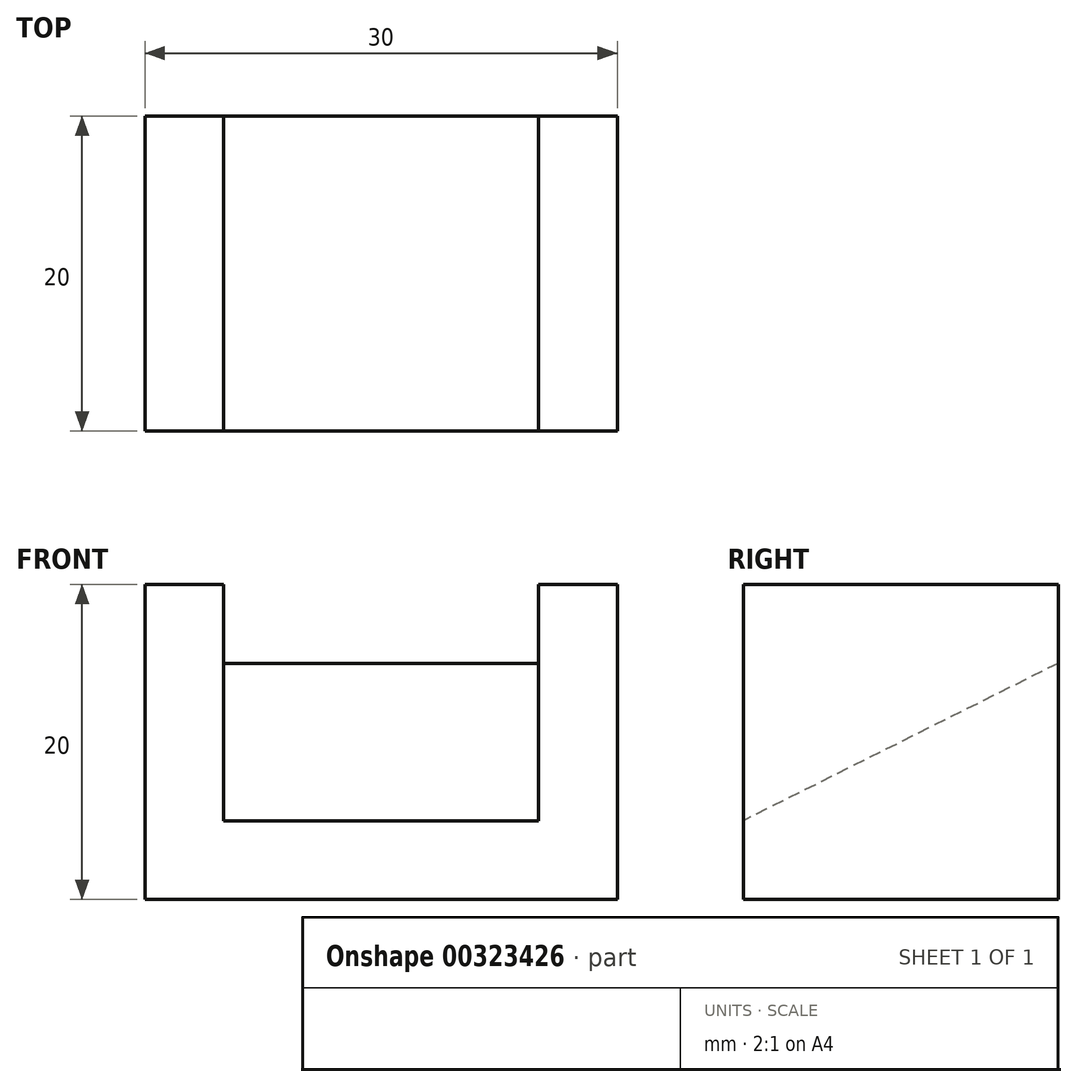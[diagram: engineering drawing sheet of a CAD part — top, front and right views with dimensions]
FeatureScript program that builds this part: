
annotation { "Feature Type Name" : "Feature", "Feature Type Description" : "" }
export const myFeature = defineFeature(function(context is Context, id is Id, definition is map)
    precondition{}
    {
        {
            var Q0;
            Q0=qCreatedBy(makeId("Front.planeOp"),FACE);
            var sketch = newSketch(context, id + "F0", { "sketchPlane" : qUnion([Q0])});
            skLineSegment(sketch, "E0.bottom", {"start": v(0, 0) * mm, "end": v(5, 0) * mm});
            skLineSegment(sketch, "E0.top", {"start": v(0, 20) * mm, "end": v(5, 20) * mm});
            skLineSegment(sketch, "E0.left", {"start": v(0, 0) * mm, "end": v(0, 20) * mm});
            skLineSegment(sketch, "E0.right", {"start": v(5, 0) * mm, "end": v(5, 20) * mm});
            skSolve(sketch);
        }
        {
            var Q0;
            Q0 = qSketchRegion(id + "F0", true);
            extrude(context, id + "F1", {"entities" : qUnion([Q0]), "depth" : 20 * mm});
        }
        {
            var Q0;
            Q0=makeQuery(id+"F1.opExtrude","SWEPT_FACE",FACE,{"disambiguationData":[OSD([sQuery(id+"F0.wireOp",EDGE,"E0.right")])]});
            var sketch = newSketch(context, id + "F2", { "sketchPlane" : qUnion([Q0])});
            skLineSegment(sketch, "E1", {"start": v(0, 15) * mm, "end": v(-20, 5) * mm});
            skLineSegment(sketch, "E2", {"start": v(-20, 5) * mm, "end": v(0, 5) * mm});
            skLineSegment(sketch, "E3", {"start": v(0, 5) * mm, "end": v(0, 15) * mm});
            skSolve(sketch);
        }
        {
            var Q0;
            Q0=makeQuery(id+"F2.imprint","IMPRINT",FACE,{"disambiguationData":[TD([[makeQuery(id+"F2.imprint","IMPRINT",EDGE,{"derivedFrom":sQuery(id+"F2.wireOp",EDGE,"E1")}),1.0]])]});
            extrude(context, id + "F3", {"entities" : qUnion([Q0]), "operationType" : NewBodyOperationType.ADD, "depth" : 20 * mm});
        }
        {
            var Q0;
            {var subQ0=sQuery(id+"F0.wireOp",EDGE,"E0.right");var subQ3=sQuery(id+"F0.wireOp",EDGE,"E0.bottom");var subQ4=makeQuery(id+"F1.opExtrude","SWEPT_FACE",FACE,{"disambiguationData":[OSD([subQ0])]});Q0=makeQuery(id+"F3.boolean.opBoolean","SPLIT",FACE,{"disambiguationData":[TD([makeQuery(id+"F1.opExtrude","SWEPT_FACE",FACE,{"disambiguationData":[OSD([subQ3])]})])],"derivedFrom":subQ4});}
            extrude(context, id + "F4", {"entities" : qUnion([Q0]), "operationType" : NewBodyOperationType.ADD, "depth" : 20 * mm});
        }
        {
            var Q0;
            Q0=makeQuery(id+"F4.boolean.opBoolean","MERGE",FACE,{"derivedFrom":[makeQuery(id+"F3.opExtrude","CAP_FACE",FACE,{"disambiguationData":[OSD([sQuery(id+"F2.wireOp",EDGE,"E1"),sQuery(id+"F2.wireOp",EDGE,"E2"),sQuery(id+"F2.wireOp",EDGE,"E3")])],"isStart":false}),makeQuery(id+"F4.opExtrude","CAP_FACE",FACE,{"disambiguationData":[OSD([sQuery(id+"F0.wireOp",EDGE,"E0.right")])],"isStart":false})]});
            var sketch = newSketch(context, id + "F5", { "sketchPlane" : qUnion([Q0])});
            skLineSegment(sketch, "E4", {"start": v(0, 0) * mm, "end": v(0, 20) * mm});
            skPoint(sketch, "E4.endSnap0", {"position": v(0, 7.5) * mm});
            skLineSegment(sketch, "E5", {"start": v(0, 20) * mm, "end": v(-20, 20) * mm});
            skLineSegment(sketch, "E6", {"start": v(-20, 20) * mm, "end": v(-20, 0) * mm});
            skLineSegment(sketch, "E7", {"start": v(-20, 0) * mm, "end": v(0, 0) * mm});
            skSolve(sketch);
        }
        {
            var Q0;
            Q0=makeQuery(id+"F4.boolean.opBoolean","MERGE",FACE,{"derivedFrom":[makeQuery(id+"F3.opExtrude","CAP_FACE",FACE,{"disambiguationData":[OSD([sQuery(id+"F2.wireOp",EDGE,"E1"),sQuery(id+"F2.wireOp",EDGE,"E2"),sQuery(id+"F2.wireOp",EDGE,"E3")])],"isStart":false}),makeQuery(id+"F4.opExtrude","CAP_FACE",FACE,{"disambiguationData":[OSD([sQuery(id+"F0.wireOp",EDGE,"E0.right")])],"isStart":false})]});
            var Q1;
            {var subQ2=sQuery(id+"F5.wireOp",EDGE,"E5");Q1=makeQuery(id+"F5.imprint","IMPRINT",FACE,{"disambiguationData":[TD([[makeQuery(id+"F5.imprint","IMPRINT",EDGE,{"derivedFrom":subQ2}),1.0]])]});}
            extrude(context, id + "F6", {"entities" : qUnion([Q0, Q1]), "operationType" : NewBodyOperationType.ADD, "depth" : 5 * mm});
        }
    });
